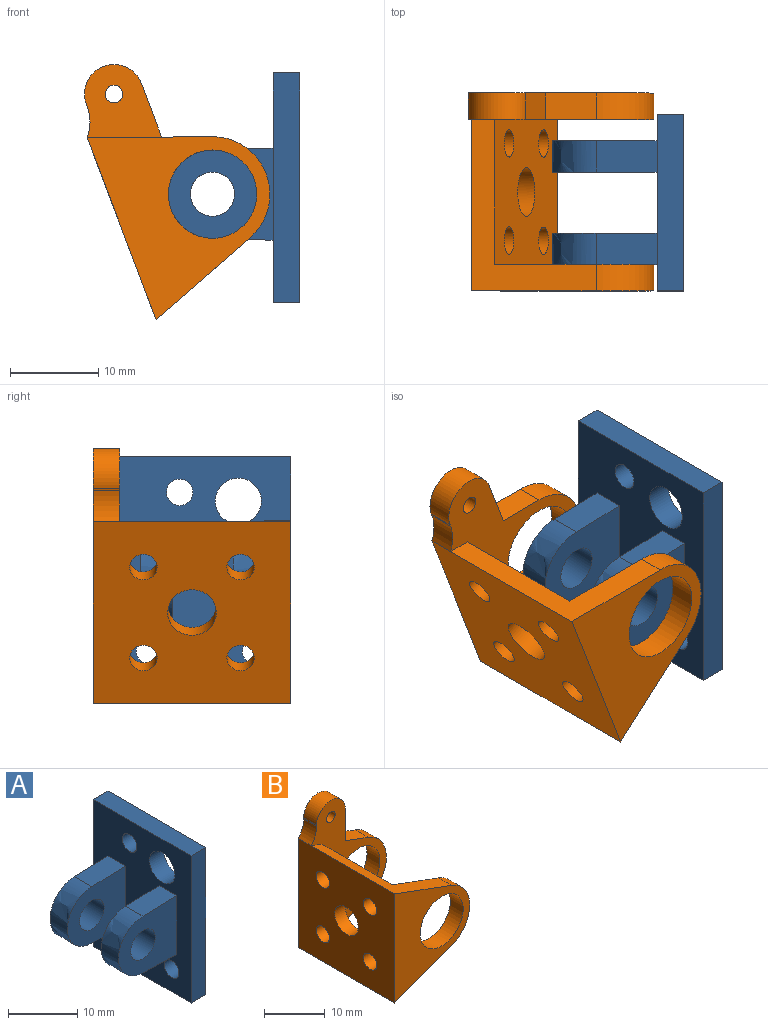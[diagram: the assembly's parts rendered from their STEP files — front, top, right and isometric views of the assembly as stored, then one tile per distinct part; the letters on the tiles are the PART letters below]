
ASSEMBLY  parts=2 mates=1
PART A: 26 faces, bbox 16.3x20x26 mm
  f0: plane 3.55x0mm, normal (-1,0,0.03), area 0mm2, adj f1,f5,f21,f24
  f1: extruded ~9.99x5mm, area 55.7mm2, adj f0,f2,f21,f24
  f2: plane 3.55x0mm, normal (-0.99,0,-0.17), area 0mm2, adj f1,f3,f21,f24
  f3: plane 6.85x3.55mm, normal (-0.03,0,-1), area 24.3mm2, adj f2,f6,f21,f24
  f4: cylinder r=2.5mm len=5mm, axis (0,1,0), area 55.8mm2, adj f21,f24
  f5: plane 6.85x3.55mm, normal (-0.03,0,1), area 24.3mm2, adj f0,f6,f21,f24
  f6: plane 26x20mm, normal (-1,0,0), area 403.4mm2, adj f3,f5,f7,f8,f9,f10,f11,f12
  f7: plane 26x3mm, normal (0,1,0), area 78mm2, adj f6,f8,f13,f14
  f8: plane 20x3mm, normal (0,0,-1), area 60mm2, adj f6,f7,f9,f14
  f9: plane 26x3mm, normal (0,-1,0), area 78mm2, adj f6,f8,f13,f14
  f10: cylinder r=1.5mm len=3mm, axis (1,0,0), area 28.3mm2, adj f6,f14
  f11: cylinder r=1.5mm len=3mm, axis (1,0,0), area 28.3mm2, adj f6,f14
  f12: cylinder r=1.5mm len=3mm, axis (1,0,0), area 28.3mm2, adj f6,f14
  f13: plane 20x3mm, normal (0,0,1), area 60mm2, adj f6,f7,f9,f14
  f14: plane 26x20mm, normal (1,0,0), area 477.4mm2, adj f7,f8,f9,f10,f11,f12,f13,f25
  f15: plane 3.55x0mm, normal (-1,0,0.03), area 0mm2, adj f16,f20,f22,f23
  f16: extruded ~9.99x5mm, area 55.7mm2, adj f15,f17,f22,f23
  f17: plane 3.55x0mm, normal (-0.99,0,-0.17), area 0mm2, adj f16,f18,f22,f23
  f18: plane 6.85x3.55mm, normal (-0.03,0,-1), area 24.3mm2, adj f6,f17,f22,f23
  f19: cylinder r=2.5mm len=5mm, axis (0,1,0), area 55.8mm2, adj f22,f23
  f20: plane 6.85x3.55mm, normal (-0.03,0,1), area 24.3mm2, adj f6,f15,f22,f23
  f21: plane 13.34x10.43mm, normal (0,-1,0), area 89.5mm2, adj f0,f1,f2,f3,f4,f5,f6
  f22: plane 13.34x10.43mm, normal (0,1,0), area 89.5mm2, adj f6,f15,f16,f17,f18,f19,f20
  f23: plane 13.34x10.43mm, normal (0,-1,0), area 89.5mm2, adj f6,f15,f16,f17,f18,f19,f20
  f24: plane 13.34x10.43mm, normal (0,1,0), area 89.5mm2, adj f0,f1,f2,f3,f4,f5,f6
  f25: cylinder r=2.61mm len=5.21mm, axis (1,0,0), area 49.1mm2, adj f6,f14
PART B: 23 faces, bbox 17.5x22.4x28.9 mm
  f0: plane 19.4x13.26mm, normal (0.35,0,0.94), area 86.1mm2, adj f2,f3,f8,f9,f11,f12
  f1: plane 5.35x3mm, normal (0.35,0,0.94), area 17.1mm2, adj f4,f7,f8,f19
  f2: plane 22.4x22mm, normal (-1,0,0), area 438.9mm2, adj f0,f6,f7,f11,f13,f14,f15,f16
  f3: plane 20.15x16.4mm, normal (1,0,0), area 276.5mm2, adj f0,f6,f8,f12,f13,f14,f15,f16
  f4: cylinder r=6.5mm len=12.19mm, axis (0,-1,0), area 47.4mm2, adj f1,f6,f7,f8
  f5: cylinder r=5mm len=10mm, axis (0,-1,0), area 94.2mm2, adj f7,f8
  f6: plane 22.4x13.26mm, normal (0.35,0,-0.94), area 128.5mm2, adj f2,f3,f4,f7,f8,f9,f11,f12
  f7: plane 28.88x17.5mm, normal (0,1,0), area 236.5mm2, adj f1,f2,f4,f5,f6,f18,f19,f20
  f8: plane 27.96x17.5mm, normal (0,-1,0), area 183.9mm2, adj f0,f1,f3,f4,f5,f6,f18,f19
  f9: cylinder r=6.5mm len=12.19mm, axis (0,1,0), area 47.4mm2, adj f0,f6,f11,f12
  f10: cylinder r=5mm len=10mm, axis (0,1,0), area 94.2mm2, adj f11,f12
  f11: plane 22x17.5mm, normal (0,-1,0), area 185.7mm2, adj f0,f2,f6,f9,f10
  f12: plane 20.15x15mm, normal (0,1,0), area 133mm2, adj f0,f3,f6,f9,f10
  f13: cylinder r=2.75mm len=5.5mm, axis (-1,0,0), area 43.2mm2, adj f2,f3
  f14: cylinder r=1.55mm len=3.1mm, axis (-1,0,0), area 24.3mm2, adj f2,f3
  f15: cylinder r=1.55mm len=3.1mm, axis (-1,0,0), area 24.3mm2, adj f2,f3
  f16: cylinder r=1.55mm len=3.1mm, axis (-1,0,0), area 24.3mm2, adj f2,f3
  f17: cylinder r=1.55mm len=3.1mm, axis (-1,0,0), area 24.3mm2, adj f2,f3
  f18: plane 3x0.25mm, normal (-1,0,0), area 0.8mm2, adj f7,f8,f21,f22
  f19: plane 6.47x3mm, normal (1,0,0), area 19.4mm2, adj f1,f7,f8,f21
  f20: cylinder r=1mm len=3mm, axis (0,1,0), area 18.8mm2, adj f7,f8
  f21: cylinder r=3.33mm len=6.67mm, axis (0,1,0), area 31.4mm2, adj f7,f8,f18,f19
  f22: cylinder r=5mm len=3.3mm, axis (0,-1,0), area 10.8mm2, adj f2,f7,f8,f18
PLACE A at identity fixed
PLACE B rot(axis=(0,-1,0),20.7deg) t=(1.12,1.2,3.7)mm
MATE revolute B.f4 <-> A.f4  axis (0,1,0) through (-9.55,123.98,4.92)mm
